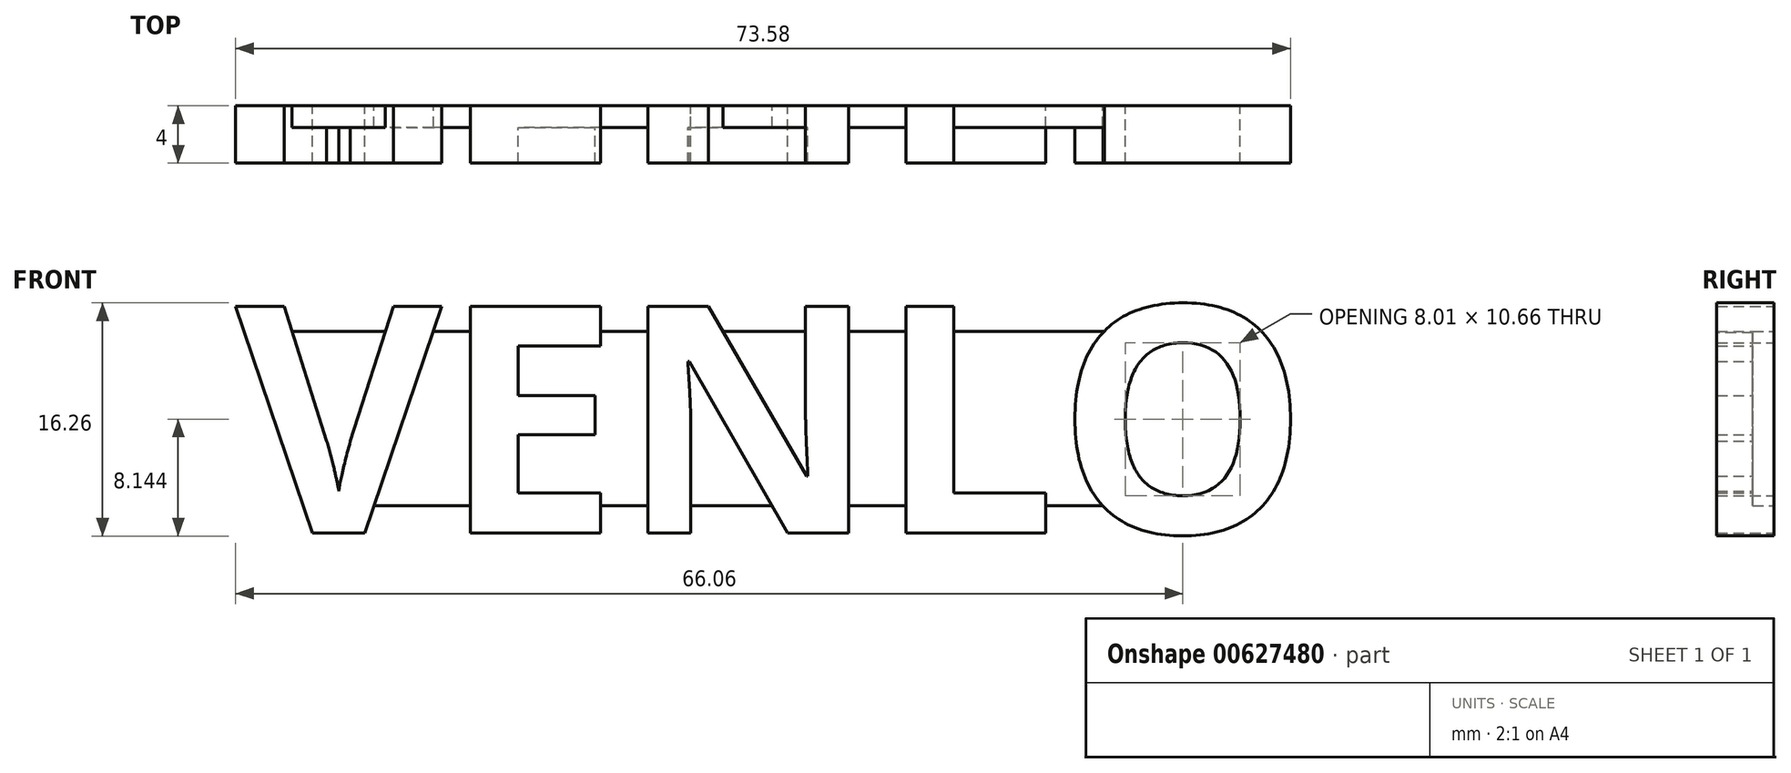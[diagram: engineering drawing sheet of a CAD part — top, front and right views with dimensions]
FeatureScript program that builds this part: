
annotation { "Feature Type Name" : "Feature", "Feature Type Description" : "" }
export const myFeature = defineFeature(function(context is Context, id is Id, definition is map)
    precondition{}
    {
        {
            var Q0;
            Q0=qCreatedBy(makeId("Front.planeOp"),FACE);
            var sketch = newSketch(context, id + "F0", { "sketchPlane" : qUnion([Q0])});
            skText(sketch, "E0", { "text": "VENLO", "fontName": "OpenSans-Bold.ttf"});
            skLineSegment(sketch, "E1", {"start": v(40.06, 5.9) * mm, "end": v(-21.41, 5.9) * mm});
            skLineSegment(sketch, "E2", {"start": v(-21.41, 5.9) * mm, "end": v(-17.36, -6.26) * mm});
            skLineSegment(sketch, "E3", {"start": v(-17.36, -6.26) * mm, "end": v(40.52, -6.26) * mm});
            skLineSegment(sketch, "E4", {"start": v(40.52, -6.26) * mm, "end": v(38.93, 0) * mm});
            skLineSegment(sketch, "E5", {"start": v(38.93, 0) * mm, "end": v(40.06, 5.9) * mm});
            const initialGuessF0  = {"E0": [-0.02208, -0.00816, 1, 0, 0.01593]};
            skSetInitialGuess(sketch, initialGuessF0);
            skSolve(sketch);
        }
        {
            var Q0;
            {var subQ1=sQuery(id+"F0.wireOp",EDGE,"E0.sketch_text.stroke-6");Q0=makeQuery(id+"F0.imprint","IMPRINT",FACE,{"disambiguationData":[TD([[makeQuery(id+"F0.imprint","IMPRINT",EDGE,{"derivedFrom":subQ1}),1.0]])]});}
            var Q1;
            {var subQ0=sQuery(id+"F0.wireOp",EDGE,"E1");var subQ1=sQuery(id+"F0.wireOp",EDGE,"E0.sketch_text.stroke-1");var subQ2=makeQuery(id+"F0.imprint","INTERSECT",VERTEX,{"derivedFrom":[subQ1,subQ0]});Q1=makeQuery(id+"F0.imprint","IMPRINT",FACE,{"disambiguationData":[TD([[makeQuery(id+"F0.imprint","IMPRINT",EDGE,{"disambiguationData":[TD([[subQ2,-1.0]])],"derivedFrom":subQ1}),1.0]])]});}
            var Q2;
            {var subQ10=sQuery(id+"F0.wireOp",EDGE,"E0.sketch_text.stroke-14");Q2=makeQuery(id+"F0.imprint","IMPRINT",FACE,{"disambiguationData":[TD([[makeQuery(id+"F0.imprint","IMPRINT",EDGE,{"derivedFrom":subQ10}),1.0]])]});}
            var Q3;
            {var subQ4=sQuery(id+"F0.wireOp",EDGE,"E0.sketch_text.stroke-24");Q3=makeQuery(id+"F0.imprint","IMPRINT",FACE,{"disambiguationData":[TD([[makeQuery(id+"F0.imprint","IMPRINT",EDGE,{"derivedFrom":subQ4}),1.0]])]});}
            var Q4;
            {var subQ4=sQuery(id+"F0.wireOp",EDGE,"E0.sketch_text.stroke-31");Q4=makeQuery(id+"F0.imprint","IMPRINT",FACE,{"disambiguationData":[TD([[makeQuery(id+"F0.imprint","IMPRINT",EDGE,{"derivedFrom":subQ4}),1.0]])]});}
            var Q5;
            {var subQ0=sQuery(id+"F0.wireOp",EDGE,"E1");var subQ1=sQuery(id+"F0.wireOp",EDGE,"E0.sketch_text.stroke-35");var subQ2=makeQuery(id+"F0.imprint","INTERSECT",VERTEX,{"derivedFrom":[subQ1,subQ0]});Q5=makeQuery(id+"F0.imprint","IMPRINT",FACE,{"disambiguationData":[TD([[makeQuery(id+"F0.imprint","IMPRINT",EDGE,{"disambiguationData":[TD([[subQ2,-1.0]])],"derivedFrom":subQ1}),1.0]])]});}
            var Q6;
            {var subQ5=sQuery(id+"F0.wireOp",EDGE,"E0.sketch_text.stroke-39");Q6=makeQuery(id+"F0.imprint","IMPRINT",FACE,{"disambiguationData":[TD([[makeQuery(id+"F0.imprint","IMPRINT",EDGE,{"derivedFrom":subQ5}),1.0]])]});}
            extrude(context, id + "F1", {"entities" : qUnion([Q0, Q1, Q2, Q3, Q4, Q5, Q6]), "depth" : 1.5 * mm, "offsetDistance" : 25 * mm});
        }
        {
            var Q0;
            {var subQ1=sQuery(id+"F0.wireOp",EDGE,"E0.sketch_text.stroke-2");Q0=makeQuery(id+"F0.imprint","IMPRINT",FACE,{"disambiguationData":[TD([[makeQuery(id+"F0.imprint","IMPRINT",EDGE,{"derivedFrom":subQ1}),-1.0]])]});}
            var Q1;
            {var subQ0=sQuery(id+"F0.wireOp",EDGE,"E0.sketch_text.stroke-6");Q1=makeQuery(id+"F0.imprint","IMPRINT",FACE,{"disambiguationData":[TD([[makeQuery(id+"F0.imprint","IMPRINT",EDGE,{"derivedFrom":subQ0}),-1.0]])]});}
            var Q2;
            {var subQ0=sQuery(id+"F0.wireOp",EDGE,"E0.sketch_text.stroke-0");Q2=makeQuery(id+"F0.imprint","IMPRINT",FACE,{"disambiguationData":[TD([[makeQuery(id+"F0.imprint","IMPRINT",EDGE,{"derivedFrom":subQ0}),-1.0]])]});}
            var Q3;
            {var subQ0=sQuery(id+"F0.wireOp",EDGE,"E0.sketch_text.stroke-12");Q3=makeQuery(id+"F0.imprint","IMPRINT",FACE,{"disambiguationData":[TD([[makeQuery(id+"F0.imprint","IMPRINT",EDGE,{"derivedFrom":subQ0}),-1.0]])]});}
            var Q4;
            {var subQ8=sQuery(id+"F0.wireOp",EDGE,"E0.sketch_text.stroke-14");Q4=makeQuery(id+"F0.imprint","IMPRINT",FACE,{"disambiguationData":[TD([[makeQuery(id+"F0.imprint","IMPRINT",EDGE,{"derivedFrom":subQ8}),-1.0]])]});}
            var Q5;
            {var subQ0=sQuery(id+"F0.wireOp",EDGE,"E0.sketch_text.stroke-10");Q5=makeQuery(id+"F0.imprint","IMPRINT",FACE,{"disambiguationData":[TD([[makeQuery(id+"F0.imprint","IMPRINT",EDGE,{"derivedFrom":subQ0}),-1.0]])]});}
            var Q6;
            {var subQ0=sQuery(id+"F0.wireOp",EDGE,"E0.sketch_text.stroke-27");Q6=makeQuery(id+"F0.imprint","IMPRINT",FACE,{"disambiguationData":[TD([[makeQuery(id+"F0.imprint","IMPRINT",EDGE,{"derivedFrom":subQ0}),-1.0]])]});}
            var Q7;
            {var subQ13=sQuery(id+"F0.wireOp",EDGE,"E0.sketch_text.stroke-24");Q7=makeQuery(id+"F0.imprint","IMPRINT",FACE,{"disambiguationData":[TD([[makeQuery(id+"F0.imprint","IMPRINT",EDGE,{"derivedFrom":subQ13}),-1.0]])]});}
            var Q8;
            {var subQ0=sQuery(id+"F0.wireOp",EDGE,"E0.sketch_text.stroke-29");Q8=makeQuery(id+"F0.imprint","IMPRINT",FACE,{"disambiguationData":[TD([[makeQuery(id+"F0.imprint","IMPRINT",EDGE,{"derivedFrom":subQ0}),-1.0]])]});}
            var Q9;
            {var subQ0=sQuery(id+"F0.wireOp",EDGE,"E0.sketch_text.stroke-34");Q9=makeQuery(id+"F0.imprint","IMPRINT",FACE,{"disambiguationData":[TD([[makeQuery(id+"F0.imprint","IMPRINT",EDGE,{"derivedFrom":subQ0}),-1.0]])]});}
            var Q10;
            {var subQ0=sQuery(id+"F0.wireOp",EDGE,"E0.sketch_text.stroke-22");Q10=makeQuery(id+"F0.imprint","IMPRINT",FACE,{"disambiguationData":[TD([[makeQuery(id+"F0.imprint","IMPRINT",EDGE,{"derivedFrom":subQ0}),-1.0]])]});}
            var Q11;
            {var subQ0=sQuery(id+"F0.wireOp",EDGE,"E0.sketch_text.stroke-41");Q11=makeQuery(id+"F0.imprint","IMPRINT",FACE,{"disambiguationData":[TD([[makeQuery(id+"F0.imprint","IMPRINT",EDGE,{"derivedFrom":subQ0}),-1.0]])]});}
            var Q12;
            {var subQ1=sQuery(id+"F0.wireOp",EDGE,"E0.sketch_text.stroke-39");Q12=makeQuery(id+"F0.imprint","IMPRINT",FACE,{"disambiguationData":[TD([[makeQuery(id+"F0.imprint","IMPRINT",EDGE,{"derivedFrom":subQ1}),-1.0]])]});}
            var Q13;
            {var subQ0=sQuery(id+"F0.wireOp",EDGE,"E0.sketch_text.stroke-37");Q13=makeQuery(id+"F0.imprint","IMPRINT",FACE,{"disambiguationData":[TD([[makeQuery(id+"F0.imprint","IMPRINT",EDGE,{"derivedFrom":subQ0}),-1.0]])]});}
            var Q14;
            Q14=makeQuery(id+"F0.imprint","IMPRINT",FACE,{"disambiguationData":[TD([[makeQuery(id+"F0.imprint","IMPRINT",EDGE,{"derivedFrom":sQuery(id+"F0.wireOp",EDGE,"E0.sketch_text.stroke-42")}),-1.0]])]});
            var Q15;
            {var subQ4=sQuery(id+"F0.wireOp",EDGE,"E0.sketch_text.stroke-46");Q15=makeQuery(id+"F0.imprint","IMPRINT",FACE,{"disambiguationData":[TD([[makeQuery(id+"F0.imprint","IMPRINT",EDGE,{"derivedFrom":subQ4}),-1.0]])]});}
            extrude(context, id + "F2", {"entities" : qUnion([Q0, Q1, Q2, Q3, Q4, Q5, Q6, Q7, Q8, Q9, Q10, Q11, Q12, Q13, Q14, Q15]), "operationType" : NewBodyOperationType.ADD, "depth" : 4 * mm, "offsetDistance" : 25 * mm});
        }
    });
